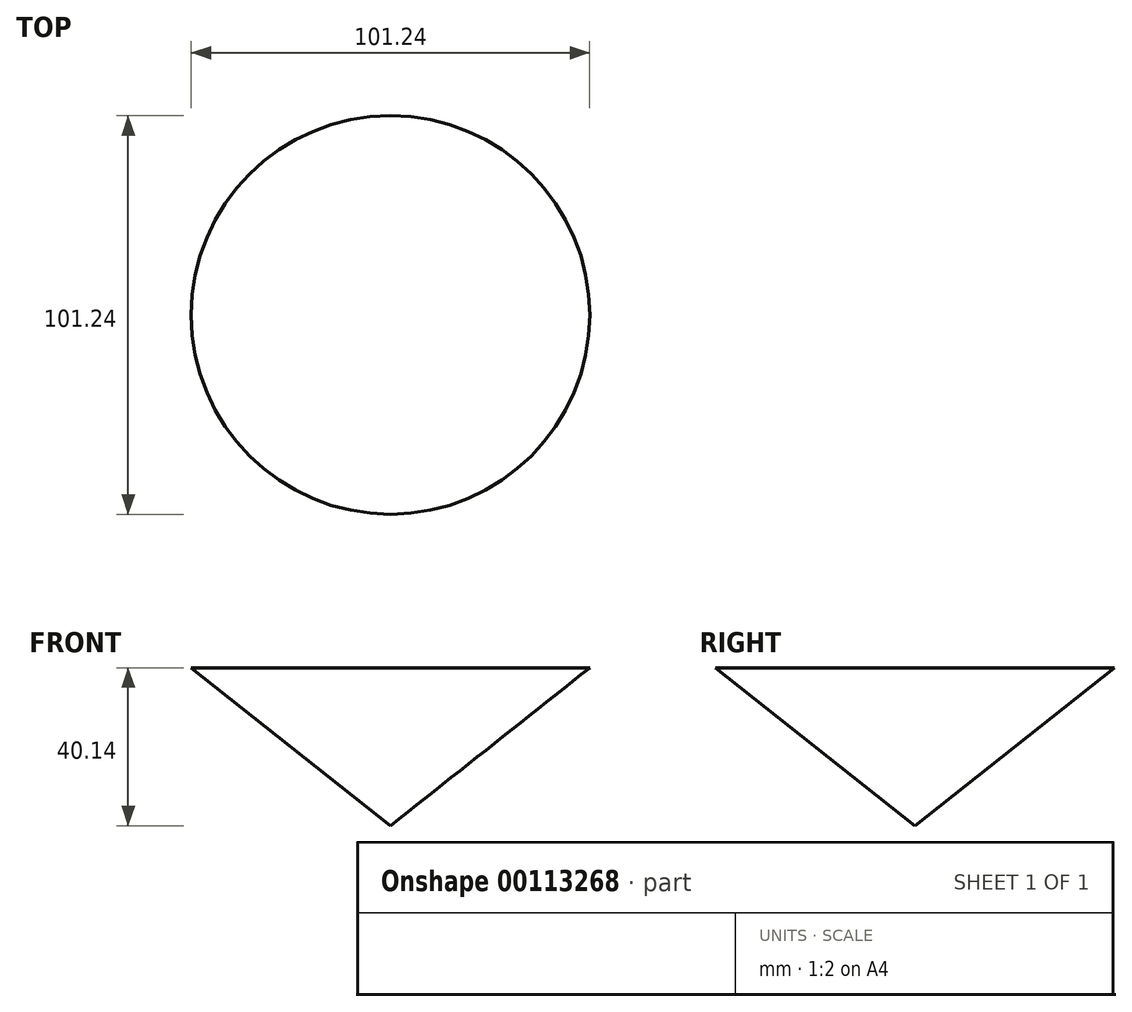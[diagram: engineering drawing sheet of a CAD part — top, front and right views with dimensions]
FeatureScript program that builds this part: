
annotation { "Feature Type Name" : "Feature", "Feature Type Description" : "" }
export const myFeature = defineFeature(function(context is Context, id is Id, definition is map)
    precondition{}
    {
        {
            var Q0;
            Q0=qCreatedBy(makeId("Front.planeOp"),FACE);
            var sketch = newSketch(context, id + "F0", { "sketchPlane" : qUnion([Q0])});
            skLineSegment(sketch, "E0", {"start": v(0, 0) * mm, "end": v(50.62, 40.14) * mm});
            skLineSegment(sketch, "E1", {"start": v(50.62, 40.14) * mm, "end": v(0, 40.14) * mm});
            skLineSegment(sketch, "E2", {"start": v(0, 40.14) * mm, "end": v(0, 0) * mm});
            skSolve(sketch);
        }
        {
            var Q0;
            Q0 = qSketchRegion(id + "F0", true);
            var Q1;
            Q1=sQuery(id+"F0.wireOp",EDGE,"E2");
            revolve(context, id + "F1", {"entities" : qUnion([Q0]), "axis" : qUnion([Q1]), "revolveType" : RevolveType.FULL});
        }
    });
